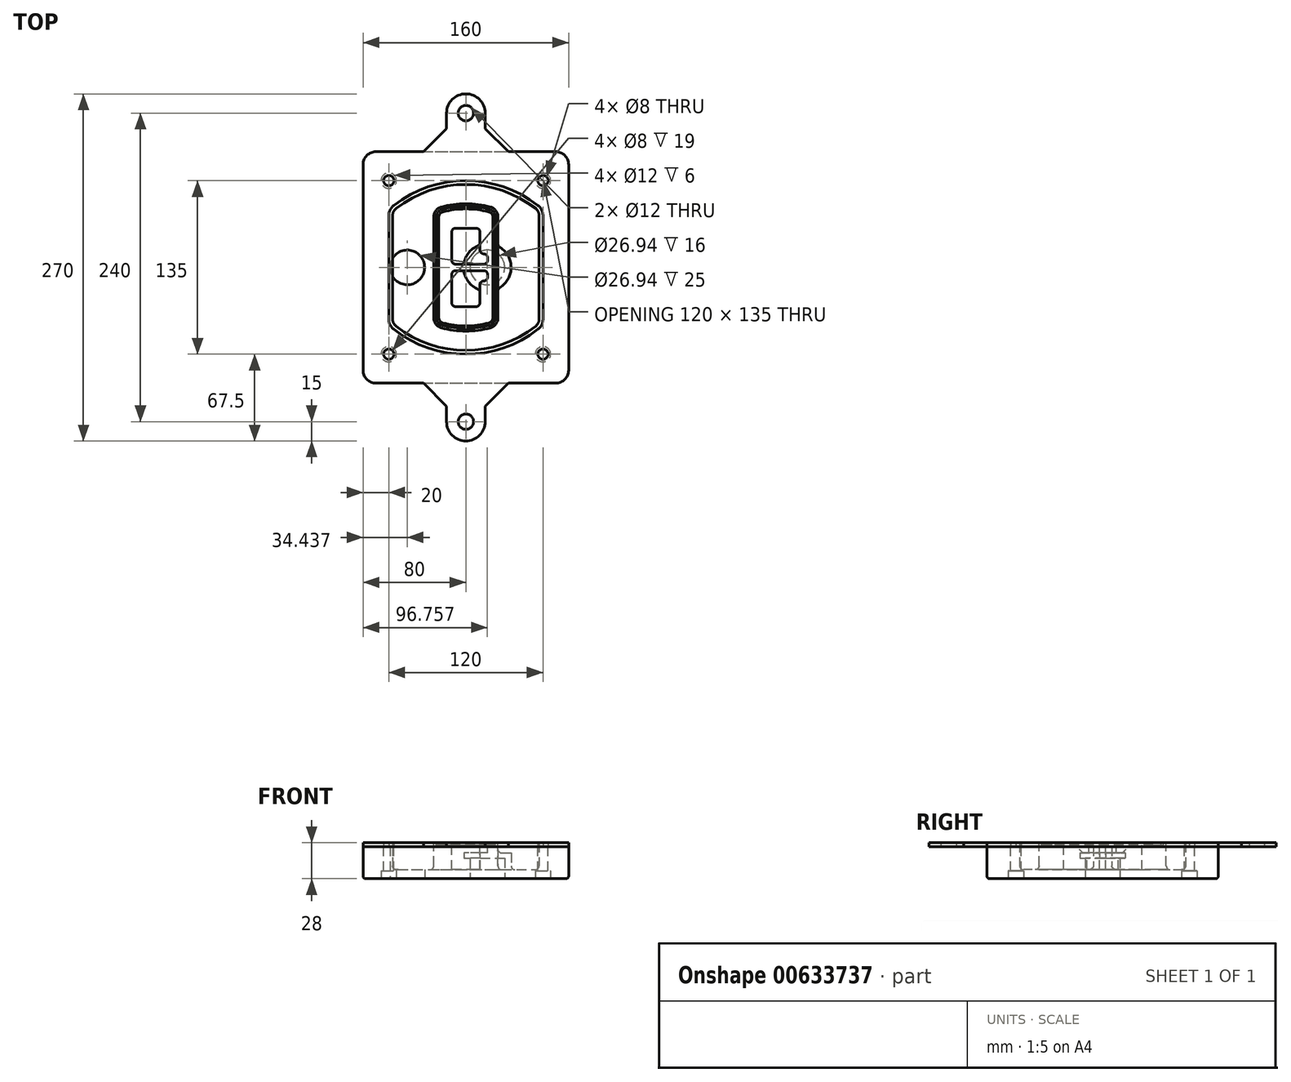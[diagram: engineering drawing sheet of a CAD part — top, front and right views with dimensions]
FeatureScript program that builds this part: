
annotation { "Feature Type Name" : "Feature", "Feature Type Description" : "" }
export const myFeature = defineFeature(function(context is Context, id is Id, definition is map)
    precondition{}
    {
        {
            var Q0;
            Q0=qCreatedBy(makeId("Top.planeOp"),FACE);
            var sketch = newSketch(context, id + "F0", { "sketchPlane" : qUnion([Q0])});
            skPoint(sketch, "E0.rect.middle", {"position": v(0, 0) * mm});
            skLineSegment(sketch, "E1.bottom", {"start": v(-70, -90) * mm, "end": v(70, -90) * mm});
            skLineSegment(sketch, "E1.top", {"start": v(-70, 90) * mm, "end": v(70, 90) * mm});
            skLineSegment(sketch, "E1.left", {"start": v(-80, -80) * mm, "end": v(-80, 80) * mm});
            skLineSegment(sketch, "E1.right", {"start": v(80, -80) * mm, "end": v(80, 80) * mm});
            skLineSegment(sketch, "E2", {"start": v(-80, 90) * mm, "end": v(80, -90) * mm, "construction": true});
            skLineSegment(sketch, "E3", {"start": v(80, 90) * mm, "end": v(-80, -90) * mm, "construction": true});
            skCircle(sketch, "E4", {"center": v(-60, 67.5) * mm, "radius": 4 * mm});
            skCircle(sketch, "E5", {"center": v(60, 67.5) * mm, "radius": 4 * mm});
            skCircle(sketch, "E6", {"center": v(60, -67.5) * mm, "radius": 4 * mm});
            skCircle(sketch, "E7", {"center": v(-60, -67.5) * mm, "radius": 4 * mm});
            skLineSegment(sketch, "E8", {"start": v(-60, 67.5) * mm, "end": v(60, 67.5) * mm, "construction": true});
            skLineSegment(sketch, "E9", {"start": v(60, 67.5) * mm, "end": v(60, -67.5) * mm, "construction": true});
            skLineSegment(sketch, "E10", {"start": v(60, -67.5) * mm, "end": v(-60, -67.5) * mm, "construction": true});
            skLineSegment(sketch, "E11", {"start": v(-60, -67.5) * mm, "end": v(-60, 67.5) * mm, "construction": true});
            skLineSegment(sketch, "E12", {"start": v(-60, 40.3) * mm, "end": v(-60, -40.3) * mm});
            skLineSegment(sketch, "E13", {"start": v(60, 40.3) * mm, "end": v(60, -40.3) * mm});
            skArc(sketch, "E14", {"start": v(56.15, 48.18) * mm, "mid": v(0, 67.5) * mm, "end": v(-56.15, 48.18) * mm});
            skArc(sketch, "E15", {"start": v(-56.15, -48.18) * mm, "mid": v(0, -67.5) * mm, "end": v(56.15, -48.18) * mm});
            skLineSegment(sketch, "E16", {"start": v(-60, 0) * mm, "end": v(60, 0) * mm, "construction": true});
            skPoint(sketch, "E17.visualSharp", {"position": v(-60, -45) * mm});
            skArc(sketch, "E17.filletArc", {"start": v(-60, -40.3) * mm, "mid": v(-58.99, -44.68) * mm, "end": v(-56.15, -48.18) * mm});
            skPoint(sketch, "E18.visualSharp", {"position": v(-60, 45) * mm});
            skArc(sketch, "E18.filletArc", {"start": v(-56.15, 48.18) * mm, "mid": v(-58.99, 44.68) * mm, "end": v(-60, 40.3) * mm});
            skPoint(sketch, "E19.visualSharp", {"position": v(60, 45) * mm});
            skArc(sketch, "E19.filletArc", {"start": v(60, 40.3) * mm, "mid": v(58.99, 44.68) * mm, "end": v(56.15, 48.18) * mm});
            skPoint(sketch, "E20.visualSharp", {"position": v(60, -45) * mm});
            skArc(sketch, "E20.filletArc", {"start": v(56.15, -48.18) * mm, "mid": v(58.99, -44.68) * mm, "end": v(60, -40.3) * mm});
            skPoint(sketch, "E21.visualSharp", {"position": v(-80, 90) * mm});
            skArc(sketch, "E21.filletArc", {"start": v(-70, 90) * mm, "mid": v(-77.07, 87.07) * mm, "end": v(-80, 80) * mm});
            skPoint(sketch, "E22.visualSharp", {"position": v(80, 90) * mm});
            skArc(sketch, "E22.filletArc", {"start": v(80, 80) * mm, "mid": v(77.07, 87.07) * mm, "end": v(70, 90) * mm});
            skPoint(sketch, "E23.visualSharp", {"position": v(80, -90) * mm});
            skArc(sketch, "E23.filletArc", {"start": v(70, -90) * mm, "mid": v(77.07, -87.07) * mm, "end": v(80, -80) * mm});
            skPoint(sketch, "E24.visualSharp", {"position": v(-80, -90) * mm});
            skArc(sketch, "E24.filletArc", {"start": v(-80, -80) * mm, "mid": v(-77.07, -87.07) * mm, "end": v(-70, -90) * mm});
            skArc(sketch, "E25.0", {"start": v(57, 40.3) * mm, "mid": v(56.3, 43.36) * mm, "end": v(54.3, 45.81) * mm});
            skLineSegment(sketch, "E25.1", {"start": v(57, 40.3) * mm, "end": v(57, -40.3) * mm});
            skArc(sketch, "E25.2", {"start": v(54.3, -45.81) * mm, "mid": v(56.3, -43.36) * mm, "end": v(57, -40.3) * mm});
            skArc(sketch, "E25.3", {"start": v(-54.3, -45.81) * mm, "mid": v(0, -64.5) * mm, "end": v(54.3, -45.81) * mm});
            skArc(sketch, "E25.4", {"start": v(-57, -40.3) * mm, "mid": v(-56.3, -43.36) * mm, "end": v(-54.3, -45.81) * mm});
            skArc(sketch, "E25.5", {"start": v(54.3, 45.81) * mm, "mid": v(0, 64.5) * mm, "end": v(-54.3, 45.81) * mm});
            skLineSegment(sketch, "E25.6", {"start": v(-57, 40.3) * mm, "end": v(-57, -40.3) * mm});
            skArc(sketch, "E25.7", {"start": v(-54.3, 45.81) * mm, "mid": v(-56.3, 43.36) * mm, "end": v(-57, 40.3) * mm});
            skArc(sketch, "E26.0", {"start": v(-58.62, 51.33) * mm, "mid": v(-62.58, 46.43) * mm, "end": v(-64, 40.3) * mm});
            skArc(sketch, "E26.1", {"start": v(58.62, 51.33) * mm, "mid": v(0, 71.5) * mm, "end": v(-58.62, 51.33) * mm});
            skArc(sketch, "E26.2", {"start": v(64, 40.3) * mm, "mid": v(62.58, 46.43) * mm, "end": v(58.62, 51.33) * mm});
            skLineSegment(sketch, "E26.3", {"start": v(64, 40.3) * mm, "end": v(64, -40.3) * mm});
            skArc(sketch, "E26.4", {"start": v(58.62, -51.33) * mm, "mid": v(62.58, -46.43) * mm, "end": v(64, -40.3) * mm});
            skLineSegment(sketch, "E26.5", {"start": v(-64, 40.3) * mm, "end": v(-64, -40.3) * mm});
            skArc(sketch, "E26.6", {"start": v(-58.62, -51.33) * mm, "mid": v(0, -71.5) * mm, "end": v(58.62, -51.33) * mm});
            skArc(sketch, "E26.7", {"start": v(-64, -40.3) * mm, "mid": v(-62.58, -46.43) * mm, "end": v(-58.62, -51.33) * mm});
            skSolve(sketch);
        }
        {
            var Q0;
            Q0=makeQuery(id+"F0.imprint","IMPRINT",FACE,{"disambiguationData":[TD([[makeQuery(id+"F0.imprint","IMPRINT",EDGE,{"derivedFrom":sQuery(id+"F0.wireOp",EDGE,"E1.bottom")}),1.0]])]});
            var Q1;
            Q1=makeQuery(id+"F0.imprint","IMPRINT",FACE,{"disambiguationData":[TD([[makeQuery(id+"F0.imprint","IMPRINT",EDGE,{"derivedFrom":sQuery(id+"F0.wireOp",EDGE,"E12")}),1.0]])]});
            var Q2;
            Q2=makeQuery(id+"F0.imprint","IMPRINT",FACE,{"disambiguationData":[TD([[makeQuery(id+"F0.imprint","IMPRINT",EDGE,{"derivedFrom":sQuery(id+"F0.wireOp",EDGE,"E25.0")}),1.0]])]});
            var Q3;
            Q3=makeQuery(id+"F0.imprint","IMPRINT",FACE,{"disambiguationData":[TD([[makeQuery(id+"F0.imprint","IMPRINT",EDGE,{"derivedFrom":sQuery(id+"F0.wireOp",EDGE,"E12")}),-1.0]])]});
            extrude(context, id + "F1", {"entities" : qUnion([Q0, Q1, Q2, Q3]), "oppositeDirection" : true, "depth" : 25 * mm});
        }
        {
            var Q0;
            Q0=makeQuery(id+"F0.imprint","IMPRINT",FACE,{"disambiguationData":[TD([[makeQuery(id+"F0.imprint","IMPRINT",EDGE,{"derivedFrom":sQuery(id+"F0.wireOp",EDGE,"E12")}),1.0]])]});
            extrude(context, id + "F2", {"entities" : qUnion([Q0]), "operationType" : NewBodyOperationType.ADD, "depth" : 3 * mm});
        }
        {
            var Q0;
            Q0=makeQuery(id+"F0.imprint","IMPRINT",FACE,{"disambiguationData":[TD([[makeQuery(id+"F0.imprint","IMPRINT",EDGE,{"derivedFrom":sQuery(id+"F0.wireOp",EDGE,"E25.0")}),1.0]])]});
            extrude(context, id + "F3", {"entities" : qUnion([Q0]), "operationType" : NewBodyOperationType.REMOVE, "oppositeDirection" : true, "depth" : 18 * mm});
        }
        {
            var Q0;
            Q0=makeQuery(id+"F2.opExtrude","CAP_FACE",FACE,{"disambiguationData":[OSD([sQuery(id+"F0.wireOp",EDGE,"E12"),sQuery(id+"F0.wireOp",EDGE,"E13"),sQuery(id+"F0.wireOp",EDGE,"E14"),sQuery(id+"F0.wireOp",EDGE,"E15"),sQuery(id+"F0.wireOp",EDGE,"E17.filletArc"),sQuery(id+"F0.wireOp",EDGE,"E18.filletArc"),sQuery(id+"F0.wireOp",EDGE,"E19.filletArc"),sQuery(id+"F0.wireOp",EDGE,"E20.filletArc"),sQuery(id+"F0.wireOp",EDGE,"E25.0"),sQuery(id+"F0.wireOp",EDGE,"E25.1"),sQuery(id+"F0.wireOp",EDGE,"E25.2"),sQuery(id+"F0.wireOp",EDGE,"E25.3"),sQuery(id+"F0.wireOp",EDGE,"E25.4"),sQuery(id+"F0.wireOp",EDGE,"E25.5"),sQuery(id+"F0.wireOp",EDGE,"E25.6"),sQuery(id+"F0.wireOp",EDGE,"E25.7")])],"isStart":false});
            var sketch = newSketch(context, id + "F4", { "sketchPlane" : qUnion([Q0])});
            skArc(sketch, "E27.0", {"start": v(-19.08, -46.97) * mm, "mid": v(0, -49.5) * mm, "end": v(19.08, -46.97) * mm});
            skArc(sketch, "E28.0", {"start": v(19.08, 46.97) * mm, "mid": v(0, 49.5) * mm, "end": v(-19.08, 46.97) * mm});
            skLineSegment(sketch, "E29", {"start": v(-25, 39.25) * mm, "end": v(-25, -39.25) * mm});
            skLineSegment(sketch, "E30", {"start": v(25, 39.25) * mm, "end": v(25, -39.25) * mm});
            skLineSegment(sketch, "E31", {"start": v(-25, 45.1) * mm, "end": v(25, 45.1) * mm, "construction": true});
            skLineSegment(sketch, "E32", {"start": v(-25, -45.1) * mm, "end": v(25, -45.1) * mm, "construction": true});
            skPoint(sketch, "E33.visualSharp", {"position": v(-25, 45.1) * mm});
            skArc(sketch, "E33.filletArc", {"start": v(-19.08, 46.97) * mm, "mid": v(-23.35, 44.11) * mm, "end": v(-25, 39.25) * mm});
            skPoint(sketch, "E34.visualSharp", {"position": v(25, 45.1) * mm});
            skArc(sketch, "E34.filletArc", {"start": v(25, 39.25) * mm, "mid": v(23.35, 44.11) * mm, "end": v(19.08, 46.97) * mm});
            skPoint(sketch, "E35.visualSharp", {"position": v(25, -45.1) * mm});
            skArc(sketch, "E35.filletArc", {"start": v(19.08, -46.97) * mm, "mid": v(23.35, -44.11) * mm, "end": v(25, -39.25) * mm});
            skPoint(sketch, "E36.visualSharp", {"position": v(-25, -45.1) * mm});
            skArc(sketch, "E36.filletArc", {"start": v(-25, -39.25) * mm, "mid": v(-23.35, -44.11) * mm, "end": v(-19.08, -46.97) * mm});
            skArc(sketch, "E37.0", {"start": v(54.3, 45.81) * mm, "mid": v(0, 64.5) * mm, "end": v(-54.3, 45.81) * mm});
            skArc(sketch, "E37.1", {"start": v(-54.3, 45.81) * mm, "mid": v(-56.3, 43.36) * mm, "end": v(-57, 40.3) * mm});
            skLineSegment(sketch, "E37.2", {"start": v(-57, 40.3) * mm, "end": v(-57, -40.3) * mm});
            skArc(sketch, "E37.3", {"start": v(-57, -40.3) * mm, "mid": v(-56.3, -43.36) * mm, "end": v(-54.3, -45.81) * mm});
            skArc(sketch, "E37.4", {"start": v(-54.3, -45.81) * mm, "mid": v(0, -64.5) * mm, "end": v(54.3, -45.81) * mm});
            skArc(sketch, "E37.5", {"start": v(54.3, -45.81) * mm, "mid": v(56.3, -43.36) * mm, "end": v(57, -40.3) * mm});
            skLineSegment(sketch, "E37.6", {"start": v(57, 40.3) * mm, "end": v(57, -40.3) * mm});
            skArc(sketch, "E37.7", {"start": v(57, 40.3) * mm, "mid": v(56.3, 43.36) * mm, "end": v(54.3, 45.81) * mm});
            skLineSegment(sketch, "E38.0", {"start": v(23, 39.25) * mm, "end": v(23, -39.25) * mm});
            skArc(sketch, "E38.1", {"start": v(18.56, -45.04) * mm, "mid": v(21.76, -42.9) * mm, "end": v(23, -39.25) * mm});
            skArc(sketch, "E38.2", {"start": v(-18.56, -45.04) * mm, "mid": v(0, -47.5) * mm, "end": v(18.56, -45.04) * mm});
            skArc(sketch, "E38.3", {"start": v(-23, -39.25) * mm, "mid": v(-21.76, -42.9) * mm, "end": v(-18.56, -45.04) * mm});
            skLineSegment(sketch, "E38.4", {"start": v(-23, 39.25) * mm, "end": v(-23, -39.25) * mm});
            skArc(sketch, "E38.5", {"start": v(23, 39.25) * mm, "mid": v(21.76, 42.9) * mm, "end": v(18.56, 45.04) * mm});
            skArc(sketch, "E38.6", {"start": v(-18.56, 45.04) * mm, "mid": v(-21.76, 42.9) * mm, "end": v(-23, 39.25) * mm});
            skArc(sketch, "E38.7", {"start": v(18.56, 45.04) * mm, "mid": v(0, 47.5) * mm, "end": v(-18.56, 45.04) * mm});
            skArc(sketch, "E39.0", {"start": v(21, 39.25) * mm, "mid": v(20.18, 41.68) * mm, "end": v(18.04, 43.1) * mm});
            skLineSegment(sketch, "E39.1", {"start": v(21, 39.25) * mm, "end": v(21, -39.25) * mm});
            skArc(sketch, "E39.2", {"start": v(18.04, -43.1) * mm, "mid": v(20.18, -41.68) * mm, "end": v(21, -39.25) * mm});
            skArc(sketch, "E39.3", {"start": v(-18.04, -43.1) * mm, "mid": v(0, -45.5) * mm, "end": v(18.04, -43.1) * mm});
            skArc(sketch, "E39.4", {"start": v(-21, -39.25) * mm, "mid": v(-20.18, -41.68) * mm, "end": v(-18.04, -43.1) * mm});
            skArc(sketch, "E39.5", {"start": v(18.04, 43.1) * mm, "mid": v(0, 45.5) * mm, "end": v(-18.04, 43.1) * mm});
            skLineSegment(sketch, "E39.6", {"start": v(-21, 39.25) * mm, "end": v(-21, -39.25) * mm});
            skArc(sketch, "E39.7", {"start": v(-18.04, 43.1) * mm, "mid": v(-20.18, 41.68) * mm, "end": v(-21, 39.25) * mm});
            skLineSegment(sketch, "E40", {"start": v(-25, 0) * mm, "end": v(25, 0) * mm, "construction": true});
            skLineSegment(sketch, "E41", {"start": v(-11, 5.5) * mm, "end": v(-11, 27.5) * mm});
            skLineSegment(sketch, "E42", {"start": v(-8, 30.5) * mm, "end": v(8, 30.5) * mm});
            skLineSegment(sketch, "E43", {"start": v(11, 27.5) * mm, "end": v(11, 13.5) * mm});
            skLineSegment(sketch, "E44", {"start": v(14, 10.5) * mm, "end": v(14, 10.5) * mm});
            skLineSegment(sketch, "E45", {"start": v(17, 7.5) * mm, "end": v(17, 5.5) * mm});
            skLineSegment(sketch, "E46", {"start": v(14, 2.5) * mm, "end": v(-8, 2.5) * mm});
            skPoint(sketch, "E47.visualSharp", {"position": v(-11, 30.5) * mm});
            skArc(sketch, "E47.filletArc", {"start": v(-8, 30.5) * mm, "mid": v(-10.12, 29.62) * mm, "end": v(-11, 27.5) * mm});
            skPoint(sketch, "E48.visualSharp", {"position": v(11, 30.5) * mm});
            skArc(sketch, "E48.filletArc", {"start": v(11, 27.5) * mm, "mid": v(10.12, 29.62) * mm, "end": v(8, 30.5) * mm});
            skPoint(sketch, "E49.visualSharp", {"position": v(11, 10.5) * mm});
            skArc(sketch, "E49.filletArc", {"start": v(11, 13.5) * mm, "mid": v(11.88, 11.38) * mm, "end": v(14, 10.5) * mm});
            skPoint(sketch, "E50.visualSharp", {"position": v(17, 10.5) * mm});
            skArc(sketch, "E50.filletArc", {"start": v(17, 7.5) * mm, "mid": v(16.12, 9.62) * mm, "end": v(14, 10.5) * mm});
            skPoint(sketch, "E51.visualSharp", {"position": v(17, 2.5) * mm});
            skArc(sketch, "E51.filletArc", {"start": v(14, 2.5) * mm, "mid": v(16.12, 3.38) * mm, "end": v(17, 5.5) * mm});
            skPoint(sketch, "E52.visualSharp", {"position": v(-11, 2.5) * mm});
            skArc(sketch, "E52.filletArc", {"start": v(-11, 5.5) * mm, "mid": v(-10.12, 3.38) * mm, "end": v(-8, 2.5) * mm});
            skLineSegment(sketch, "E53.0.MirrorCS", {"start": v(14, -2.5) * mm, "end": v(-8, -2.5) * mm});
            skArc(sketch, "E54.0.MirrorCS", {"start": v(-11, -5.5) * mm, "mid": v(-10.12, -3.38) * mm, "end": v(-8, -2.5) * mm});
            skLineSegment(sketch, "E55.0.MirrorCS", {"start": v(-11, -5.5) * mm, "end": v(-11, -27.5) * mm});
            skArc(sketch, "E56.0.MirrorCS", {"start": v(-8, -30.5) * mm, "mid": v(-10.12, -29.62) * mm, "end": v(-11, -27.5) * mm});
            skLineSegment(sketch, "E57.0.MirrorCS", {"start": v(-8, -30.5) * mm, "end": v(8, -30.5) * mm});
            skArc(sketch, "E58.0.MirrorCS", {"start": v(11, -27.5) * mm, "mid": v(10.12, -29.62) * mm, "end": v(8, -30.5) * mm});
            skLineSegment(sketch, "E59.0.MirrorCS", {"start": v(11, -27.5) * mm, "end": v(11, -13.5) * mm});
            skArc(sketch, "E60.0.MirrorCS", {"start": v(11, -13.5) * mm, "mid": v(11.88, -11.38) * mm, "end": v(14, -10.5) * mm});
            skArc(sketch, "E61.0.MirrorCS", {"start": v(17, -7.5) * mm, "mid": v(16.12, -9.62) * mm, "end": v(14, -10.5) * mm});
            skLineSegment(sketch, "E62.0.MirrorCS", {"start": v(17, -7.5) * mm, "end": v(17, -5.5) * mm});
            skArc(sketch, "E63.0.MirrorCS", {"start": v(14, -2.5) * mm, "mid": v(16.12, -3.38) * mm, "end": v(17, -5.5) * mm});
            skSolve(sketch);
        }
        {
            var Q0;
            Q0=makeQuery(id+"F4.imprint","IMPRINT",FACE,{"disambiguationData":[TD([[makeQuery(id+"F4.imprint","IMPRINT",EDGE,{"derivedFrom":sQuery(id+"F4.wireOp",EDGE,"E27.0")}),1.0]])]});
            var Q1;
            Q1=makeQuery(id+"F4.imprint","IMPRINT",FACE,{"disambiguationData":[TD([[makeQuery(id+"F4.imprint","IMPRINT",EDGE,{"derivedFrom":sQuery(id+"F4.wireOp",EDGE,"E38.0")}),-1.0]])]});
            var Q2;
            Q2=makeQuery(id+"F4.imprint","IMPRINT",FACE,{"disambiguationData":[TD([[makeQuery(id+"F4.imprint","IMPRINT",EDGE,{"derivedFrom":sQuery(id+"F4.wireOp",EDGE,"E39.0")}),1.0]])]});
            extrude(context, id + "F5", {"entities" : qUnion([Q0, Q1, Q2]), "operationType" : NewBodyOperationType.ADD, "endBound" : BoundingType.UP_TO_NEXT, "oppositeDirection" : true, "depth" : 25 * mm});
        }
        {
            var Q0;
            Q0=makeQuery(id+"F4.imprint","IMPRINT",FACE,{"disambiguationData":[TD([[makeQuery(id+"F4.imprint","IMPRINT",EDGE,{"derivedFrom":sQuery(id+"F4.wireOp",EDGE,"E38.0")}),-1.0]])]});
            extrude(context, id + "F6", {"entities" : qUnion([Q0]), "operationType" : NewBodyOperationType.REMOVE, "oppositeDirection" : true, "depth" : 2 * mm});
        }
        {
            var Q0;
            Q0=makeQuery(id+"F1.opExtrude","CAP_FACE",FACE,{"disambiguationData":[OSD([sQuery(id+"F0.wireOp",EDGE,"E1.bottom"),sQuery(id+"F0.wireOp",EDGE,"E1.top"),sQuery(id+"F0.wireOp",EDGE,"E1.left"),sQuery(id+"F0.wireOp",EDGE,"E1.right"),sQuery(id+"F0.wireOp",EDGE,"E4"),sQuery(id+"F0.wireOp",EDGE,"E5"),sQuery(id+"F0.wireOp",EDGE,"E6"),sQuery(id+"F0.wireOp",EDGE,"E7"),sQuery(id+"F0.wireOp",EDGE,"E21.filletArc"),sQuery(id+"F0.wireOp",EDGE,"E22.filletArc"),sQuery(id+"F0.wireOp",EDGE,"E23.filletArc"),sQuery(id+"F0.wireOp",EDGE,"E24.filletArc")])],"isStart":false});
            var sketch = newSketch(context, id + "F7", { "sketchPlane" : qUnion([Q0])});
            skCircle(sketch, "E64", {"center": v(16.76, 0) * mm, "radius": 13.47 * mm});
            skCircle(sketch, "E65", {"center": v(-45.56, 0) * mm, "radius": 13.47 * mm});
            skLineSegment(sketch, "E66", {"start": v(80, 0) * mm, "end": v(-80, 0) * mm});
            skCircle(sketch, "E67", {"center": v(16.76, 0) * mm, "radius": 18.47 * mm});
            skCircle(sketch, "E68", {"center": v(60, -67.5) * mm, "radius": 6 * mm});
            skCircle(sketch, "E69", {"center": v(-60, -67.5) * mm, "radius": 6 * mm});
            skCircle(sketch, "E70", {"center": v(-60, 67.5) * mm, "radius": 6 * mm});
            skCircle(sketch, "E71", {"center": v(60, 67.5) * mm, "radius": 6 * mm});
            skSolve(sketch);
        }
        {
            var Q0;
            {var subQ1=sQuery(id+"F7.wireOp",EDGE,"E66");var subQ4=sQuery(id+"F7.wireOp",EDGE,"E64");var subQ6=makeQuery(id+"F7.imprint","INTERSECT",VERTEX,{"disambiguationData":[OD(0.0)],"derivedFrom":[subQ4,subQ1]});Q0=makeQuery(id+"F7.imprint","IMPRINT",FACE,{"disambiguationData":[TD([[makeQuery(id+"F7.imprint","IMPRINT",EDGE,{"disambiguationData":[TD([[subQ6,-1.0]])],"derivedFrom":subQ4}),-1.0]])]});}
            var Q1;
            {var subQ0=sQuery(id+"F7.wireOp",EDGE,"E66");var subQ1=sQuery(id+"F7.wireOp",EDGE,"E64");var subQ3=makeQuery(id+"F7.imprint","INTERSECT",VERTEX,{"disambiguationData":[OD(0.0)],"derivedFrom":[subQ1,subQ0]});Q1=makeQuery(id+"F7.imprint","IMPRINT",FACE,{"disambiguationData":[TD([[makeQuery(id+"F7.imprint","IMPRINT",EDGE,{"disambiguationData":[TD([[subQ3,-1.0]])],"derivedFrom":subQ1}),1.0]])]});}
            var Q2;
            {var subQ0=sQuery(id+"F7.wireOp",EDGE,"E66");var subQ1=sQuery(id+"F7.wireOp",EDGE,"E64");var subQ3=makeQuery(id+"F7.imprint","INTERSECT",VERTEX,{"disambiguationData":[OD(0.0)],"derivedFrom":[subQ1,subQ0]});Q2=makeQuery(id+"F7.imprint","IMPRINT",FACE,{"disambiguationData":[TD([[makeQuery(id+"F7.imprint","IMPRINT",EDGE,{"disambiguationData":[TD([[subQ3,1.0]])],"derivedFrom":subQ1}),1.0]])]});}
            var Q3;
            {var subQ1=sQuery(id+"F7.wireOp",EDGE,"E66");var subQ4=sQuery(id+"F7.wireOp",EDGE,"E64");var subQ6=makeQuery(id+"F7.imprint","INTERSECT",VERTEX,{"disambiguationData":[OD(0.0)],"derivedFrom":[subQ4,subQ1]});Q3=makeQuery(id+"F7.imprint","IMPRINT",FACE,{"disambiguationData":[TD([[makeQuery(id+"F7.imprint","IMPRINT",EDGE,{"disambiguationData":[TD([[subQ6,1.0]])],"derivedFrom":subQ4}),-1.0]])]});}
            extrude(context, id + "F8", {"entities" : qUnion([Q0, Q1, Q2, Q3]), "operationType" : NewBodyOperationType.ADD, "oppositeDirection" : true, "depth" : 20 * mm});
        }
        {
            var Q0;
            {var subQ0=sQuery(id+"F7.wireOp",EDGE,"E66");var subQ1=sQuery(id+"F7.wireOp",EDGE,"E64");var subQ3=makeQuery(id+"F7.imprint","INTERSECT",VERTEX,{"disambiguationData":[OD(0.0)],"derivedFrom":[subQ1,subQ0]});Q0=makeQuery(id+"F7.imprint","IMPRINT",FACE,{"disambiguationData":[TD([[makeQuery(id+"F7.imprint","IMPRINT",EDGE,{"disambiguationData":[TD([[subQ3,-1.0]])],"derivedFrom":subQ1}),1.0]])]});}
            var Q1;
            {var subQ0=sQuery(id+"F7.wireOp",EDGE,"E66");var subQ1=sQuery(id+"F7.wireOp",EDGE,"E64");var subQ3=makeQuery(id+"F7.imprint","INTERSECT",VERTEX,{"disambiguationData":[OD(0.0)],"derivedFrom":[subQ1,subQ0]});Q1=makeQuery(id+"F7.imprint","IMPRINT",FACE,{"disambiguationData":[TD([[makeQuery(id+"F7.imprint","IMPRINT",EDGE,{"disambiguationData":[TD([[subQ3,1.0]])],"derivedFrom":subQ1}),1.0]])]});}
            extrude(context, id + "F9", {"entities" : qUnion([Q0, Q1]), "operationType" : NewBodyOperationType.REMOVE, "oppositeDirection" : true, "depth" : 16 * mm});
        }
        {
            var Q0;
            {var subQ0=sQuery(id+"F7.wireOp",EDGE,"E66");var subQ1=sQuery(id+"F7.wireOp",EDGE,"E65");var subQ3=makeQuery(id+"F7.imprint","INTERSECT",VERTEX,{"disambiguationData":[OD(0.0)],"derivedFrom":[subQ1,subQ0]});Q0=makeQuery(id+"F7.imprint","IMPRINT",FACE,{"disambiguationData":[TD([[makeQuery(id+"F7.imprint","IMPRINT",EDGE,{"disambiguationData":[TD([[subQ3,-1.0]])],"derivedFrom":subQ1}),1.0]])]});}
            var Q1;
            {var subQ0=sQuery(id+"F7.wireOp",EDGE,"E66");var subQ1=sQuery(id+"F7.wireOp",EDGE,"E65");var subQ3=makeQuery(id+"F7.imprint","INTERSECT",VERTEX,{"disambiguationData":[OD(0.0)],"derivedFrom":[subQ1,subQ0]});Q1=makeQuery(id+"F7.imprint","IMPRINT",FACE,{"disambiguationData":[TD([[makeQuery(id+"F7.imprint","IMPRINT",EDGE,{"disambiguationData":[TD([[subQ3,1.0]])],"derivedFrom":subQ1}),1.0]])]});}
            extrude(context, id + "F10", {"entities" : qUnion([Q0, Q1]), "operationType" : NewBodyOperationType.REMOVE, "oppositeDirection" : true, "depth" : 25 * mm});
        }
        {
            var Q0;
            Q0=makeQuery(id+"F7.imprint","IMPRINT",FACE,{"disambiguationData":[TD([[makeQuery(id+"F7.imprint","IMPRINT",EDGE,{"derivedFrom":sQuery(id+"F7.wireOp",EDGE,"E68")}),1.0]])]});
            var Q1;
            Q1=makeQuery(id+"F7.imprint","IMPRINT",FACE,{"disambiguationData":[TD([[makeQuery(id+"F7.imprint","IMPRINT",EDGE,{"derivedFrom":makeQuery(id+"F1.opExtrude","CAP_EDGE",EDGE,{"disambiguationData":[OSD([sQuery(id+"F0.wireOp",EDGE,"E5")])],"isStart":false})}),-1.0]])]});
            var Q2;
            Q2=makeQuery(id+"F7.imprint","IMPRINT",FACE,{"disambiguationData":[TD([[makeQuery(id+"F7.imprint","IMPRINT",EDGE,{"derivedFrom":sQuery(id+"F7.wireOp",EDGE,"E69")}),1.0]])]});
            var Q3;
            Q3=makeQuery(id+"F7.imprint","IMPRINT",FACE,{"disambiguationData":[TD([[makeQuery(id+"F7.imprint","IMPRINT",EDGE,{"derivedFrom":makeQuery(id+"F1.opExtrude","CAP_EDGE",EDGE,{"disambiguationData":[OSD([sQuery(id+"F0.wireOp",EDGE,"E4")])],"isStart":false})}),-1.0]])]});
            var Q4;
            Q4=makeQuery(id+"F7.imprint","IMPRINT",FACE,{"disambiguationData":[TD([[makeQuery(id+"F7.imprint","IMPRINT",EDGE,{"derivedFrom":sQuery(id+"F7.wireOp",EDGE,"E70")}),1.0]])]});
            var Q5;
            Q5=makeQuery(id+"F7.imprint","IMPRINT",FACE,{"disambiguationData":[TD([[makeQuery(id+"F7.imprint","IMPRINT",EDGE,{"derivedFrom":makeQuery(id+"F1.opExtrude","CAP_EDGE",EDGE,{"disambiguationData":[OSD([sQuery(id+"F0.wireOp",EDGE,"E7")])],"isStart":false})}),-1.0]])]});
            var Q6;
            Q6=makeQuery(id+"F7.imprint","IMPRINT",FACE,{"disambiguationData":[TD([[makeQuery(id+"F7.imprint","IMPRINT",EDGE,{"derivedFrom":sQuery(id+"F7.wireOp",EDGE,"E71")}),1.0]])]});
            var Q7;
            Q7=makeQuery(id+"F7.imprint","IMPRINT",FACE,{"disambiguationData":[TD([[makeQuery(id+"F7.imprint","IMPRINT",EDGE,{"derivedFrom":makeQuery(id+"F1.opExtrude","CAP_EDGE",EDGE,{"disambiguationData":[OSD([sQuery(id+"F0.wireOp",EDGE,"E6")])],"isStart":false})}),-1.0]])]});
            extrude(context, id + "F11", {"entities" : qUnion([Q0, Q1, Q2, Q3, Q4, Q5, Q6, Q7]), "operationType" : NewBodyOperationType.REMOVE, "oppositeDirection" : true, "depth" : 6 * mm});
        }
        {
            var Q0;
            Q0=makeQuery(id+"F9.boolean.opBoolean","COPY",FACE,{"derivedFrom":makeQuery(id+"F9.opExtrude","CAP_FACE",FACE,{"disambiguationData":[OSD([sQuery(id+"F7.wireOp",EDGE,"E64")])],"isStart":false})});
            var sketch = newSketch(context, id + "F12", { "sketchPlane" : qUnion([Q0])});
            skArc(sketch, "E72.0", {"start": v(11, 17.55) * mm, "mid": v(2.57, 11.82) * mm, "end": v(-1.54, 2.5) * mm});
            skArc(sketch, "E72.1", {"start": v(-1.54, -2.5) * mm, "mid": v(2.57, -11.82) * mm, "end": v(11, -17.55) * mm});
            skLineSegment(sketch, "E73", {"start": v(-1.54, -2.5) * mm, "end": v(14, -2.5) * mm});
            skLineSegment(sketch, "E74.0", {"start": v(14, 2.5) * mm, "end": v(-1.54, 2.5) * mm});
            skArc(sketch, "E74.1", {"start": v(14, 2.5) * mm, "mid": v(16.12, 3.38) * mm, "end": v(17, 5.5) * mm});
            skLineSegment(sketch, "E74.2", {"start": v(17, 7.5) * mm, "end": v(17, 5.5) * mm});
            skArc(sketch, "E74.3", {"start": v(17, 7.5) * mm, "mid": v(16.12, 9.62) * mm, "end": v(14, 10.5) * mm});
            skArc(sketch, "E74.4", {"start": v(11, 13.5) * mm, "mid": v(11.88, 11.38) * mm, "end": v(14, 10.5) * mm});
            skLineSegment(sketch, "E74.5", {"start": v(11, 17.55) * mm, "end": v(11, 13.5) * mm});
            skLineSegment(sketch, "E74.7", {"start": v(14, -2.5) * mm, "end": v(-1.54, -2.5) * mm});
            skArc(sketch, "E74.8", {"start": v(14, -2.5) * mm, "mid": v(16.12, -3.38) * mm, "end": v(17, -5.5) * mm});
            skLineSegment(sketch, "E74.9", {"start": v(17, -7.5) * mm, "end": v(17, -5.5) * mm});
            skArc(sketch, "E74.10", {"start": v(17, -7.5) * mm, "mid": v(16.12, -9.62) * mm, "end": v(14, -10.5) * mm});
            skArc(sketch, "E74.11", {"start": v(11, -13.5) * mm, "mid": v(11.88, -11.38) * mm, "end": v(14, -10.5) * mm});
            skLineSegment(sketch, "E74.12", {"start": v(11, -17.55) * mm, "end": v(11, -13.5) * mm});
            skPoint(sketch, "E75.orphan", {"position": v(11, -27.5) * mm});
            skPoint(sketch, "E76.orphan", {"position": v(-8, -2.5) * mm});
            skPoint(sketch, "E77.orphan", {"position": v(-8, 2.5) * mm});
            skPoint(sketch, "E78.orphan", {"position": v(11, 27.5) * mm});
            skSolve(sketch);
        }
        {
            var Q0;
            {var subQ7=sQuery(id+"F12.wireOp",EDGE,"E72.0");var subQ14=sQuery(id+"F12.wireOp",EDGE,"E72.1");var subQ16=sQuery(id+"F12.wireOp",EDGE,"E74.1");var subQ18=sQuery(id+"F12.wireOp",EDGE,"E74.8");Q0=qUnion([makeQuery(id+"F12.imprint","IMPRINT",FACE,{"disambiguationData":[TD([[makeQuery(id+"F12.imprint","IMPRINT",EDGE,{"derivedFrom":subQ7}),1.0]])]}),makeQuery(id+"F12.imprint","IMPRINT",FACE,{"disambiguationData":[TD([[makeQuery(id+"F12.imprint","IMPRINT",EDGE,{"derivedFrom":subQ14}),1.0]])]}),makeQuery(id+"F12.imprint","IMPRINT",FACE,{"disambiguationData":[TD([[makeQuery(id+"F12.imprint","IMPRINT",EDGE,{"derivedFrom":subQ16}),1.0]])]}),makeQuery(id+"F12.imprint","IMPRINT",FACE,{"disambiguationData":[TD([[makeQuery(id+"F12.imprint","IMPRINT",EDGE,{"derivedFrom":subQ18}),-1.0]])]})]);}
            var Q1;
            Q1=makeQuery(id+"F5.boolean.opBoolean","SPLIT",FACE,{"disambiguationData":[TD([makeQuery(id+"F5.opExtrude","SWEPT_FACE",FACE,{"disambiguationData":[OSD([sQuery(id+"F4.wireOp",EDGE,"E41")])]})])],"derivedFrom":makeQuery(id+"F3.boolean.opBoolean","COPY",FACE,{"derivedFrom":makeQuery(id+"F3.opExtrude","CAP_FACE",FACE,{"disambiguationData":[OSD([sQuery(id+"F0.wireOp",EDGE,"E25.0"),sQuery(id+"F0.wireOp",EDGE,"E25.1"),sQuery(id+"F0.wireOp",EDGE,"E25.2"),sQuery(id+"F0.wireOp",EDGE,"E25.3"),sQuery(id+"F0.wireOp",EDGE,"E25.4"),sQuery(id+"F0.wireOp",EDGE,"E25.5"),sQuery(id+"F0.wireOp",EDGE,"E25.6"),sQuery(id+"F0.wireOp",EDGE,"E25.7")])],"isStart":false})})});
            extrude(context, id + "F13", {"entities" : qUnion([Q0]), "operationType" : NewBodyOperationType.REMOVE, "endBound" : BoundingType.UP_TO_SURFACE, "endBoundEntityFace" : qUnion([Q1]), "depth" : 25 * mm});
        }
        {
            var Q0;
            Q0=makeQuery(id+"F3.boolean.opBoolean","COPY",EDGE,{"derivedFrom":makeQuery(id+"F3.opExtrude","CAP_EDGE",EDGE,{"disambiguationData":[OSD([sQuery(id+"F0.wireOp",EDGE,"E25.6")])],"isStart":false})});
            var Q1;
            Q1=makeQuery(id+"F8.boolean.opBoolean","INTERSECT",EDGE,{"derivedFrom":[makeQuery(id+"F5.opExtrude","SWEPT_FACE",FACE,{"disambiguationData":[OSD([sQuery(id+"F4.wireOp",EDGE,"E30")])]}),makeQuery(id+"F8.opExtrude","CAP_FACE",FACE,{"disambiguationData":[OSD([sQuery(id+"F7.wireOp",EDGE,"E67")])],"isStart":false})]});
            var Q2;
            Q2=makeQuery(id+"F8.boolean.opBoolean","INTERSECT",EDGE,{"disambiguationData":[OD(1.0)],"derivedFrom":[makeQuery(id+"F5.opExtrude","SWEPT_FACE",FACE,{"disambiguationData":[OSD([sQuery(id+"F4.wireOp",EDGE,"E30")])]}),makeQuery(id+"F8.opExtrude","SWEPT_FACE",FACE,{"disambiguationData":[OSD([sQuery(id+"F7.wireOp",EDGE,"E67")])]})]});
            var Q3;
            {var subQ0=sQuery(id+"F4.wireOp",EDGE,"E30");Q3=makeQuery(id+"F8.boolean.opBoolean","SPLIT",EDGE,{"disambiguationData":[TD([makeQuery(id+"F5.opExtrude","SWEPT_FACE",FACE,{"disambiguationData":[OSD([sQuery(id+"F4.wireOp",EDGE,"E35.filletArc")])]})])],"derivedFrom":makeQuery(id+"F5.opExtrude","CAP_EDGE",EDGE,{"disambiguationData":[OSD([subQ0])],"isStart":false})});}
            var Q4;
            {var subQ0=sQuery(id+"F0.wireOp",EDGE,"E25.7");var subQ1=sQuery(id+"F0.wireOp",EDGE,"E25.1");var subQ2=sQuery(id+"F0.wireOp",EDGE,"E25.6");var subQ3=sQuery(id+"F0.wireOp",EDGE,"E25.5");var subQ4=sQuery(id+"F0.wireOp",EDGE,"E25.4");var subQ5=sQuery(id+"F0.wireOp",EDGE,"E25.0");var subQ6=sQuery(id+"F0.wireOp",EDGE,"E25.2");var subQ7=sQuery(id+"F0.wireOp",EDGE,"E25.3");Q4=makeQuery(id+"F8.boolean.opBoolean","INTERSECT",EDGE,{"derivedFrom":[makeQuery(id+"F5.boolean.opBoolean","SPLIT",FACE,{"disambiguationData":[TD([makeQuery(id+"F2.opExtrude","SWEPT_FACE",FACE,{"disambiguationData":[OSD([subQ5])]})])],"derivedFrom":makeQuery(id+"F3.boolean.opBoolean","COPY",FACE,{"derivedFrom":makeQuery(id+"F3.opExtrude","CAP_FACE",FACE,{"disambiguationData":[OSD([subQ5,subQ1,subQ6,subQ7,subQ4,subQ3,subQ2,subQ0])],"isStart":false})})}),makeQuery(id+"F8.opExtrude","SWEPT_FACE",FACE,{"disambiguationData":[OSD([sQuery(id+"F7.wireOp",EDGE,"E67")])]})]});}
            var Q5;
            Q5=makeQuery(id+"F8.boolean.opBoolean","INTERSECT",EDGE,{"disambiguationData":[OD(0.0)],"derivedFrom":[makeQuery(id+"F5.opExtrude","SWEPT_FACE",FACE,{"disambiguationData":[OSD([sQuery(id+"F4.wireOp",EDGE,"E30")])]}),makeQuery(id+"F8.opExtrude","SWEPT_FACE",FACE,{"disambiguationData":[OSD([sQuery(id+"F7.wireOp",EDGE,"E67")])]})]});
            fillet(context, id + "F14", {"entities" : qUnion([Q0, Q1, Q2, Q3, Q4, Q5]), "radius" : 3 * mm, "tangentPropagation" : true, "allowEdgeOverflow" : false});
        }
        {
            var Q0;
            Q0=makeQuery(id+"F1.opExtrude","CAP_EDGE",EDGE,{"disambiguationData":[OSD([sQuery(id+"F0.wireOp",EDGE,"E1.bottom")])],"isStart":false});
            fillet(context, id + "F15", {"entities" : qUnion([Q0]), "radius" : 2 * mm, "tangentPropagation" : true, "allowEdgeOverflow" : false});
        }
        {
            var Q0;
            {var subQ0=sQuery(id+"F0.wireOp",EDGE,"E21.filletArc");var subQ1=sQuery(id+"F0.wireOp",EDGE,"E7");var subQ2=sQuery(id+"F0.wireOp",EDGE,"E6");var subQ3=sQuery(id+"F0.wireOp",EDGE,"E5");var subQ4=sQuery(id+"F0.wireOp",EDGE,"E4");var subQ5=sQuery(id+"F0.wireOp",EDGE,"E22.filletArc");var subQ6=sQuery(id+"F0.wireOp",EDGE,"E1.bottom");var subQ7=sQuery(id+"F0.wireOp",EDGE,"E1.right");var subQ8=sQuery(id+"F0.wireOp",EDGE,"E1.top");var subQ9=sQuery(id+"F0.wireOp",EDGE,"E1.left");var subQ10=sQuery(id+"F0.wireOp",EDGE,"E23.filletArc");var subQ11=sQuery(id+"F0.wireOp",EDGE,"E24.filletArc");Q0=makeQuery(id+"F2.boolean.opBoolean","SPLIT",FACE,{"disambiguationData":[TD([makeQuery(id+"F1.opExtrude","SWEPT_FACE",FACE,{"disambiguationData":[OSD([subQ6])]})])],"derivedFrom":makeQuery(id+"F1.opExtrude","CAP_FACE",FACE,{"disambiguationData":[OSD([subQ6,subQ8,subQ9,subQ7,subQ4,subQ3,subQ2,subQ1,subQ0,subQ5,subQ10,subQ11])],"isStart":true})});}
            var sketch = newSketch(context, id + "F16", { "sketchPlane" : qUnion([Q0])});
            skArc(sketch, "E79", {"start": v(15, 120) * mm, "mid": v(0, 135) * mm, "end": v(-15, 120) * mm});
            skCircle(sketch, "E80", {"center": v(0, 120) * mm, "radius": 6 * mm});
            skLineSegment(sketch, "E81", {"start": v(0, 120) * mm, "end": v(0, 90) * mm, "construction": true});
            skLineSegment(sketch, "E82", {"start": v(-15, 120) * mm, "end": v(-15, 108) * mm});
            skLineSegment(sketch, "E83", {"start": v(15, 120) * mm, "end": v(15, 108) * mm});
            skLineSegment(sketch, "E84", {"start": v(-15, 108) * mm, "end": v(-33, 90) * mm});
            skLineSegment(sketch, "E85", {"start": v(15, 108) * mm, "end": v(33, 90) * mm});
            skLineSegment(sketch, "E86", {"start": v(-80, 0) * mm, "end": v(80, 0) * mm, "construction": true});
            skLineSegment(sketch, "E87.MirrorCS", {"start": v(-15, -108) * mm, "end": v(-33, -90) * mm});
            skLineSegment(sketch, "E88.MirrorCS", {"start": v(-15, -120) * mm, "end": v(-15, -108) * mm});
            skLineSegment(sketch, "E89.MirrorCS", {"start": v(15, -120) * mm, "end": v(15, -108) * mm});
            skLineSegment(sketch, "E90.MirrorCS", {"start": v(15, -108) * mm, "end": v(33, -90) * mm});
            skLineSegment(sketch, "E91.MirrorCS", {"start": v(0, -120) * mm, "end": v(0, -90) * mm, "construction": true});
            skCircle(sketch, "E92.MirrorC", {"center": v(0, -120) * mm, "radius": 6 * mm});
            skArc(sketch, "E93.MirrorCS", {"start": v(15, -120) * mm, "mid": v(0, -135) * mm, "end": v(-15, -120) * mm});
            skSolve(sketch);
        }
        {
            var Q0;
            {var subQ1=sQuery(id+"F16.wireOp",EDGE,"E87.MirrorCS");Q0=makeQuery(id+"F16.imprint","IMPRINT",FACE,{"disambiguationData":[TD([[makeQuery(id+"F16.imprint","IMPRINT",EDGE,{"derivedFrom":subQ1}),-1.0]])]});}
            var Q1;
            Q1=makeQuery(id+"F16.imprint","IMPRINT",FACE,{"disambiguationData":[TD([[makeQuery(id+"F16.imprint","IMPRINT",EDGE,{"derivedFrom":makeQuery(id+"F1.opExtrude","CAP_EDGE",EDGE,{"disambiguationData":[OSD([sQuery(id+"F0.wireOp",EDGE,"E1.left")])],"isStart":true})}),-1.0]])]});
            var Q2;
            Q2=makeQuery(id+"F16.imprint","IMPRINT",FACE,{"disambiguationData":[TD([[makeQuery(id+"F16.imprint","IMPRINT",EDGE,{"derivedFrom":sQuery(id+"F16.wireOp",EDGE,"E79")}),1.0]])]});
            var Q3;
            Q3=makeQuery(id+"F2.opExtrude","CAP_FACE",FACE,{"disambiguationData":[OSD([sQuery(id+"F0.wireOp",EDGE,"E12"),sQuery(id+"F0.wireOp",EDGE,"E13"),sQuery(id+"F0.wireOp",EDGE,"E14"),sQuery(id+"F0.wireOp",EDGE,"E15"),sQuery(id+"F0.wireOp",EDGE,"E17.filletArc"),sQuery(id+"F0.wireOp",EDGE,"E18.filletArc"),sQuery(id+"F0.wireOp",EDGE,"E19.filletArc"),sQuery(id+"F0.wireOp",EDGE,"E20.filletArc"),sQuery(id+"F0.wireOp",EDGE,"E25.0"),sQuery(id+"F0.wireOp",EDGE,"E25.1"),sQuery(id+"F0.wireOp",EDGE,"E25.2"),sQuery(id+"F0.wireOp",EDGE,"E25.3"),sQuery(id+"F0.wireOp",EDGE,"E25.4"),sQuery(id+"F0.wireOp",EDGE,"E25.5"),sQuery(id+"F0.wireOp",EDGE,"E25.6"),sQuery(id+"F0.wireOp",EDGE,"E25.7")])],"isStart":false});
            extrude(context, id + "F17", {"entities" : qUnion([Q0, Q1, Q2]), "endBound" : BoundingType.UP_TO_SURFACE, "depth" : 25 * mm, "endBoundEntityFace" : qUnion([Q3]), "offsetDistance" : 25 * mm});
        }
    });
